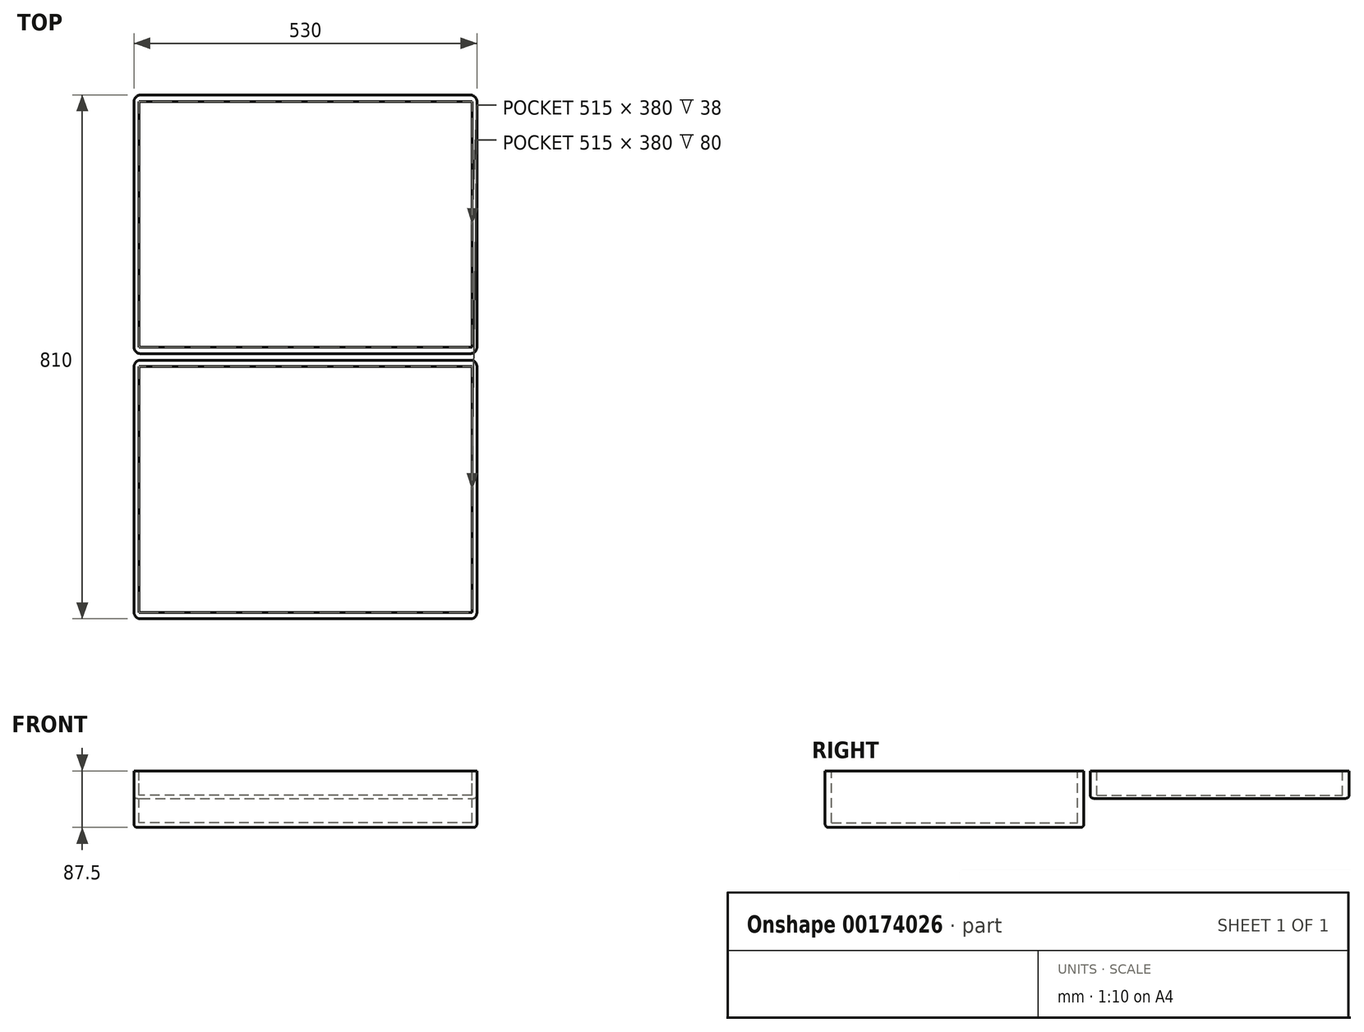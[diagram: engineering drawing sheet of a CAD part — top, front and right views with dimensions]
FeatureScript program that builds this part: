
annotation { "Feature Type Name" : "Feature", "Feature Type Description" : "" }
export const myFeature = defineFeature(function(context is Context, id is Id, definition is map)
    precondition{}
    {
        {
            var Q0;
            Q0=qCreatedBy(makeId("Top.planeOp"),FACE);
            var sketch = newSketch(context, id + "F0", { "sketchPlane" : qUnion([Q0])});
            skLineSegment(sketch, "E0.bottom", {"start": v(0, 0) * mm, "end": v(530, 0) * mm});
            skLineSegment(sketch, "E0.top", {"start": v(0, 400) * mm, "end": v(530, 400) * mm});
            skLineSegment(sketch, "E0.left", {"start": v(0, 0) * mm, "end": v(0, 400) * mm});
            skLineSegment(sketch, "E0.right", {"start": v(530, 0) * mm, "end": v(530, 400) * mm});
            skSolve(sketch);
        }
        {
            var Q0;
            Q0=makeQuery(id+"F0.imprint","IMPRINT",FACE,{"disambiguationData":[TD([[makeQuery(id+"F0.imprint","IMPRINT",EDGE,{"derivedFrom":sQuery(id+"F0.wireOp",EDGE,"E0.bottom")}),1.0]])]});
            extrude(context, id + "F1", {"entities" : qUnion([Q0]), "oppositeDirection" : true, "depth" : (80 + 7.5) * mm});
        }
        {
            var Q0;
            Q0=makeQuery(id+"F1.opExtrude","CAP_FACE",FACE,{"disambiguationData":[OSD([sQuery(id+"F0.wireOp",EDGE,"E0.bottom"),sQuery(id+"F0.wireOp",EDGE,"E0.top"),sQuery(id+"F0.wireOp",EDGE,"E0.left"),sQuery(id+"F0.wireOp",EDGE,"E0.right")])],"isStart":true});
            var sketch = newSketch(context, id + "F2", { "sketchPlane" : qUnion([Q0])});
            skLineSegment(sketch, "E1.bottom", {"start": v(0, 410) * mm, "end": v(530, 410) * mm});
            skLineSegment(sketch, "E1.top", {"start": v(0, 810) * mm, "end": v(530, 810) * mm});
            skLineSegment(sketch, "E1.left", {"start": v(0, 410) * mm, "end": v(0, 810) * mm});
            skLineSegment(sketch, "E1.right", {"start": v(530, 410) * mm, "end": v(530, 810) * mm});
            skSolve(sketch);
        }
        {
            var Q0;
            Q0=makeQuery(id+"F2.imprint","IMPRINT",FACE,{"disambiguationData":[TD([[makeQuery(id+"F2.imprint","IMPRINT",EDGE,{"derivedFrom":sQuery(id+"F2.wireOp",EDGE,"E1.bottom")}),1.0]])]});
            extrude(context, id + "F3", {"entities" : qUnion([Q0]), "oppositeDirection" : true, "depth" : (35 + 7.5) * mm});
        }
        {
            var Q0;
            Q0=makeQuery(id+"F1.opExtrude","CAP_FACE",FACE,{"disambiguationData":[OSD([sQuery(id+"F0.wireOp",EDGE,"E0.bottom"),sQuery(id+"F0.wireOp",EDGE,"E0.top"),sQuery(id+"F0.wireOp",EDGE,"E0.left"),sQuery(id+"F0.wireOp",EDGE,"E0.right")])],"isStart":true});
            var sketch = newSketch(context, id + "F4", { "sketchPlane" : qUnion([Q0])});
            skLineSegment(sketch, "E2.bottom", {"start": v(522.5, 10) * mm, "end": v(7.5, 10) * mm});
            skLineSegment(sketch, "E2.top", {"start": v(522.5, 390) * mm, "end": v(7.5, 390) * mm});
            skLineSegment(sketch, "E2.left", {"start": v(522.5, 10) * mm, "end": v(522.5, 390) * mm});
            skLineSegment(sketch, "E2.right", {"start": v(7.5, 10) * mm, "end": v(7.5, 390) * mm});
            skPoint(sketch, "E2.middle", {"position": v(265, 200) * mm});
            skSolve(sketch);
        }
        {
            var Q0;
            Q0 = qSketchRegion(id + "F4", true);
            extrude(context, id + "F5", {"entities" : qUnion([Q0]), "operationType" : NewBodyOperationType.REMOVE, "oppositeDirection" : true, "depth" : 80 * mm});
        }
        {
            var Q0;
            Q0=makeQuery(id+"F3.opExtrude","CAP_FACE",FACE,{"disambiguationData":[OSD([sQuery(id+"F2.wireOp",EDGE,"E1.bottom"),sQuery(id+"F2.wireOp",EDGE,"E1.top"),sQuery(id+"F2.wireOp",EDGE,"E1.left"),sQuery(id+"F2.wireOp",EDGE,"E1.right")])],"isStart":true});
            var sketch = newSketch(context, id + "F6", { "sketchPlane" : qUnion([Q0])});
            skLineSegment(sketch, "E3.bottom", {"start": v(522.5, 420) * mm, "end": v(7.5, 420) * mm});
            skLineSegment(sketch, "E3.top", {"start": v(522.5, 800) * mm, "end": v(7.5, 800) * mm});
            skLineSegment(sketch, "E3.left", {"start": v(522.5, 420) * mm, "end": v(522.5, 800) * mm});
            skLineSegment(sketch, "E3.right", {"start": v(7.5, 420) * mm, "end": v(7.5, 800) * mm});
            skPoint(sketch, "E3.middle", {"position": v(265, 610) * mm});
            skPoint(sketch, "E3.middle.positionSnap0", {"position": v(530, 610) * mm});
            skPoint(sketch, "E3.middle.positionSnap1", {"position": v(265, 410) * mm});
            skPoint(sketch, "E3.centerSnap0", {"position": v(530, 610) * mm});
            skPoint(sketch, "E3.centerSnap1", {"position": v(265, 410) * mm});
            skSolve(sketch);
        }
        {
            var Q0;
            Q0 = qSketchRegion(id + "F6", true);
            extrude(context, id + "F7", {"entities" : qUnion([Q0]), "operationType" : NewBodyOperationType.REMOVE, "oppositeDirection" : true, "depth" : 38 * mm});
        }
        {
            var Q0;
            Q0=makeQuery(id+"F1.opExtrude","SWEPT_EDGE",EDGE,{"disambiguationData":[OSD([sQuery(id+"F0.wireOp",EDGE,"E0.bottom"),sQuery(id+"F0.wireOp",EDGE,"E0.left")])]});
            var Q1;
            Q1=makeQuery(id+"F1.opExtrude","SWEPT_EDGE",EDGE,{"disambiguationData":[OSD([sQuery(id+"F0.wireOp",EDGE,"E0.bottom"),sQuery(id+"F0.wireOp",EDGE,"E0.right")])]});
            var Q2;
            Q2=makeQuery(id+"F1.opExtrude","SWEPT_EDGE",EDGE,{"disambiguationData":[OSD([sQuery(id+"F0.wireOp",EDGE,"E0.top"),sQuery(id+"F0.wireOp",EDGE,"E0.right")])]});
            var Q3;
            Q3=makeQuery(id+"F3.opExtrude","SWEPT_EDGE",EDGE,{"disambiguationData":[OSD([sQuery(id+"F2.wireOp",EDGE,"E1.bottom"),sQuery(id+"F2.wireOp",EDGE,"E1.right")])]});
            var Q4;
            Q4=makeQuery(id+"F1.opExtrude","SWEPT_EDGE",EDGE,{"disambiguationData":[OSD([sQuery(id+"F0.wireOp",EDGE,"E0.top"),sQuery(id+"F0.wireOp",EDGE,"E0.left")])]});
            var Q5;
            Q5=makeQuery(id+"F3.opExtrude","SWEPT_EDGE",EDGE,{"disambiguationData":[OSD([sQuery(id+"F2.wireOp",EDGE,"E1.bottom"),sQuery(id+"F2.wireOp",EDGE,"E1.left")])]});
            var Q6;
            Q6=makeQuery(id+"F3.opExtrude","SWEPT_EDGE",EDGE,{"disambiguationData":[OSD([sQuery(id+"F2.wireOp",EDGE,"E1.top"),sQuery(id+"F2.wireOp",EDGE,"E1.left")])]});
            var Q7;
            Q7=makeQuery(id+"F3.opExtrude","SWEPT_EDGE",EDGE,{"disambiguationData":[OSD([sQuery(id+"F2.wireOp",EDGE,"E1.top"),sQuery(id+"F2.wireOp",EDGE,"E1.right")])]});
            fillet(context, id + "F8", {"entities" : qUnion([Q0, Q1, Q2, Q3, Q4, Q5, Q6, Q7]), "radius" : 10 * mm, "tangentPropagation" : true, "allowEdgeOverflow" : false});
        }
        {
            var Q0;
            Q0=makeQuery(id+"F1.opExtrude","CAP_EDGE",EDGE,{"disambiguationData":[OSD([sQuery(id+"F0.wireOp",EDGE,"E0.bottom")])],"isStart":false});
            var Q1;
            Q1=makeQuery(id+"F3.opExtrude","CAP_EDGE",EDGE,{"disambiguationData":[OSD([sQuery(id+"F2.wireOp",EDGE,"E1.right")])],"isStart":false});
            fillet(context, id + "F9", {"entities" : qUnion([Q0, Q1]), "radius" : 5 * mm, "tangentPropagation" : true, "allowEdgeOverflow" : false});
        }
    });
